# Revit family: wer
name_source: partatom
category: Pipe Accessories
revit_build: Autodesk Revit 2018 (Build: 20170223_1515(x64)
units: mm (PartAtom-declared; Revit-internal decimal feet)

## family parameters
Cut with Voids When Loaded = No
Host = Face
OmniClass Number = 23.27.43.00
OmniClass Title = Pipe Fittings
Part Type = Normal
Round Connector Dimension = Use Diameter
Shared = No

## types (6) — shared parameters
Assembly Code = D2040100
BIMobject category = Joints
Default Elevation = 1219.2 mm
Description = Collars made in technopolymeric with m6 nut
Design country = Italy
Edition number = 1
IFC Classification = Pipe Fitting
Keynote = 15410
Lookup Table Name = Collars-Made-Technopolymeric-With-M6-Nut-90815
Manufacturer = Aignep Spa
Manufacturer country = Italy
Manufacturer name = Aignep Spa
Material main = Plastic
Model = 90815
OmniClass Code = 23-27 43 00
OmniClass Description = Pipe Fittings
Product Guid = 4f9a4926-dc38-41e9-a2af-7cd52319e393
Product Material = AIGNEP - Plastic - Black
Product SKU = Collars-Made-In-Technopolymeric-With-M6-Nut-90815
Product certification = https://www.aignep.com
Product data url = https://www.bimobject.com
Product family = INFINITY
Product group = Fittings
Product name = Collars Made In Technopolymeric With M6 Nut - 90815
Product url = https://www.aignep.com
QR code = https://www.bimobject.com
Tick Size = 32 mm  [stored 0.104987 ft]
URL = https://www.aignep.com

## per-type parameters (varying)
| type | A | B | C | D | D1 | Diameter Inside | Diameter Outside | Distance | Geometry Bottom | Nominal Diameter | Profile | Radius |
| D 20 | 15 mm  [stored 0.0492126 ft] | 35.5 mm  [stored 0.11647 ft] | 26 mm | 17 mm  [stored 0.0557743 ft] | 9.4 mm  [stored 0.0308399 ft] | 21 mm | 27 mm | 3.6 mm  [stored 0.011811 ft] | Yes | 20  [stored 0.0656168 ft] | 16.64 mm  [stored 0.0545932 ft] | 13.5 mm |
| D 25 | 17 mm  [stored 0.0557743 ft] | 39.5 mm | 26 mm | 22 mm  [stored 0.0721785 ft] | 8 mm  [stored 0.0262467 ft] | 25 mm  [stored 0.082021 ft] | 31 mm  [stored 0.101706 ft] | 3.6 mm  [stored 0.011811 ft] | Yes | 25  [stored 0.082021 ft] | 20 mm  [stored 0.0656168 ft] | 15.5 mm  [stored 0.050853 ft] |
| D 32 | 20 mm  [stored 0.0656168 ft] | 44.5 mm  [stored 0.145997 ft] | 40 mm  [stored 0.131234 ft] | 25 mm  [stored 0.082021 ft] | 10.93 mm  [stored 0.0358596 ft] | 31 mm  [stored 0.101706 ft] | 37 mm | 3.6 mm  [stored 0.011811 ft] | Yes | 32  [stored 0.104987 ft] | 24 mm  [stored 0.0787402 ft] | 18.5 mm |
| D 40 | 24.5 mm  [stored 0.0803806 ft] | 53.5 mm  [stored 0.175525 ft] | 40 mm  [stored 0.131234 ft] | 32 mm  [stored 0.104987 ft] | 13.29 mm  [stored 0.0436024 ft] | 40 mm  [stored 0.131234 ft] | 46 mm  [stored 0.150919 ft] | 0 mm  [stored 0 ft] | No | 40  [stored 0.131234 ft] | 24 mm  [stored 0.0787402 ft] | 23 mm  [stored 0.0754593 ft] |
| D 50 | 30 mm  [stored 0.0984252 ft] | 62 mm | 54 mm  [stored 0.177165 ft] | 42 mm  [stored 0.137795 ft] | 23.05 mm  [stored 0.0756234 ft] | 51 mm  [stored 0.167323 ft] | 57 mm | 0 mm  [stored 0 ft] | No | 50  [stored 0.164042 ft] | 24 mm  [stored 0.0787402 ft] | 28.5 mm |
| D 63 | 36 mm  [stored 0.11811 ft] | 73.5 mm | 54 mm  [stored 0.177165 ft] | 50 mm  [stored 0.164042 ft] | 14.2 mm  [stored 0.0465879 ft] | 63 mm | 69 mm | 0 mm  [stored 0 ft] | No | 63 | 24 mm  [stored 0.0787402 ft] | 34.5 mm  [stored 0.113189 ft] |

note: [stored X ft] marks values corroborated as IEEE doubles in the binary element streams (Revit-internal decimal feet)

## geometry (parser evidence)
native form markers: Sweep x3
no freeform markers — native parametric forms only
